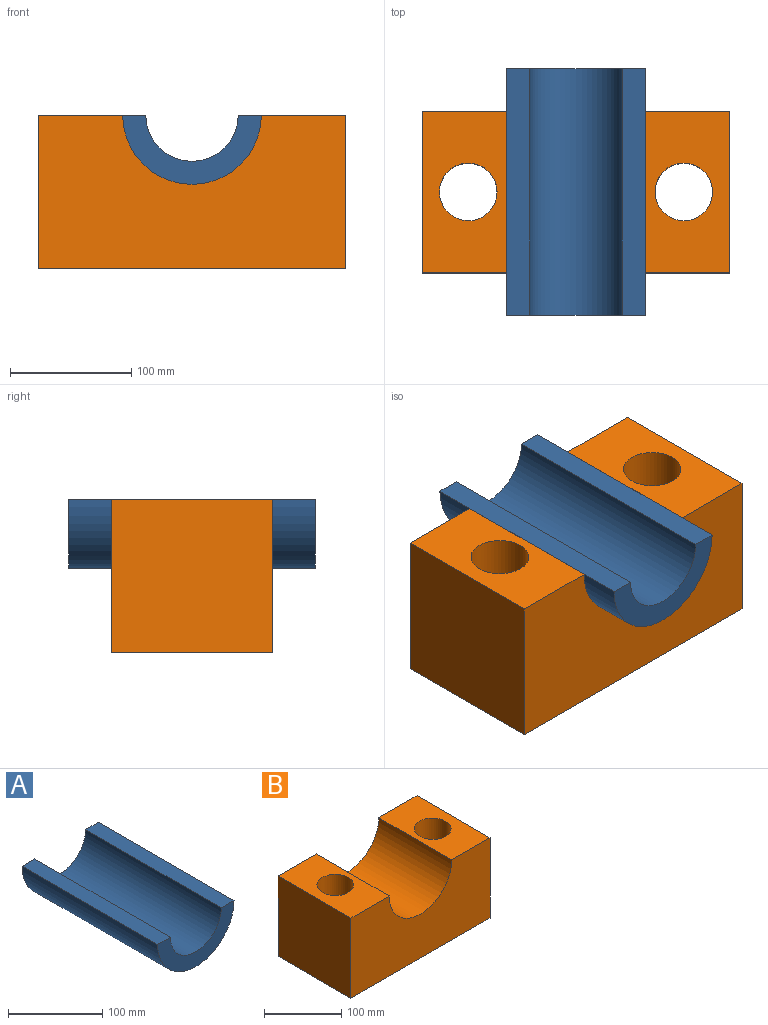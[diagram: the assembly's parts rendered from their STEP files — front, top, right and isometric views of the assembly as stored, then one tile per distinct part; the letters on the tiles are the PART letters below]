
ASSEMBLY  parts=2 mates=1
PART A: 6 faces, bbox 114.3x203.2x57.2 mm
  f0: plane 203.2x19.05mm, normal (0,0,1), area 3871mm2, adj f1,f2,f3,f4
  f1: plane 114.3x57.15mm, normal (0,1,0), area 2850.2mm2, adj f0,f3,f4,f5
  f2: plane 114.3x57.15mm, normal (0,-1,0), area 2850.2mm2, adj f0,f3,f4,f5
  f3: cylinder r=57.15mm len=203.2mm, axis (0,1,0), area 36482.9mm2, adj f0,f1,f2,f5
  f4: cylinder r=38.1mm len=203.2mm, axis (0,1,0), area 24322mm2, adj f0,f1,f2,f5
  f5: plane 203.2x19.05mm, normal (0,0,1), area 3871mm2, adj f1,f2,f3,f4
PART B: 10 faces, bbox 254x133.4x127 mm
  f0: plane 133.35x69.85mm, normal (0,0,1), area 7542.6mm2, adj f2,f3,f4,f6,f9
  f1: plane 133.35x127mm, normal (1,0,0), area 16935.5mm2, adj f2,f6,f7,f8
  f2: plane 254x127mm, normal (0,1,0), area 27127.6mm2, adj f0,f1,f3,f7,f8,f9
  f3: plane 133.35x127mm, normal (-1,0,0), area 16935.5mm2, adj f0,f2,f6,f8
  f4: cylinder r=23.75mm len=127mm, axis (0,0,-1), area 18950.9mm2, adj f0,f8
  f5: cylinder r=23.75mm len=127mm, axis (0,0,-1), area 18950.9mm2, adj f7,f8
  f6: plane 254x127mm, normal (0,-1,0), area 27127.6mm2, adj f0,f1,f3,f7,f8,f9
  f7: plane 133.35x69.85mm, normal (0,0,1), area 7542.6mm2, adj f1,f2,f5,f6,f9
  f8: plane 254x133.35mm, normal (0,0,-1), area 30327.1mm2, adj f1,f2,f3,f4,f5,f6
  f9: cylinder r=57.15mm len=133.35mm, axis (0,-1,0), area 23941.9mm2, adj f0,f2,f6,f7
PLACE A t=(40.58,109.23,168.33)mm
PLACE B t=(40.58,109.23,41.33)mm
MATE fastened B.f9 <-> A.f3  axis (0,-1,0) through (40.58,109.23,168.33)mm
